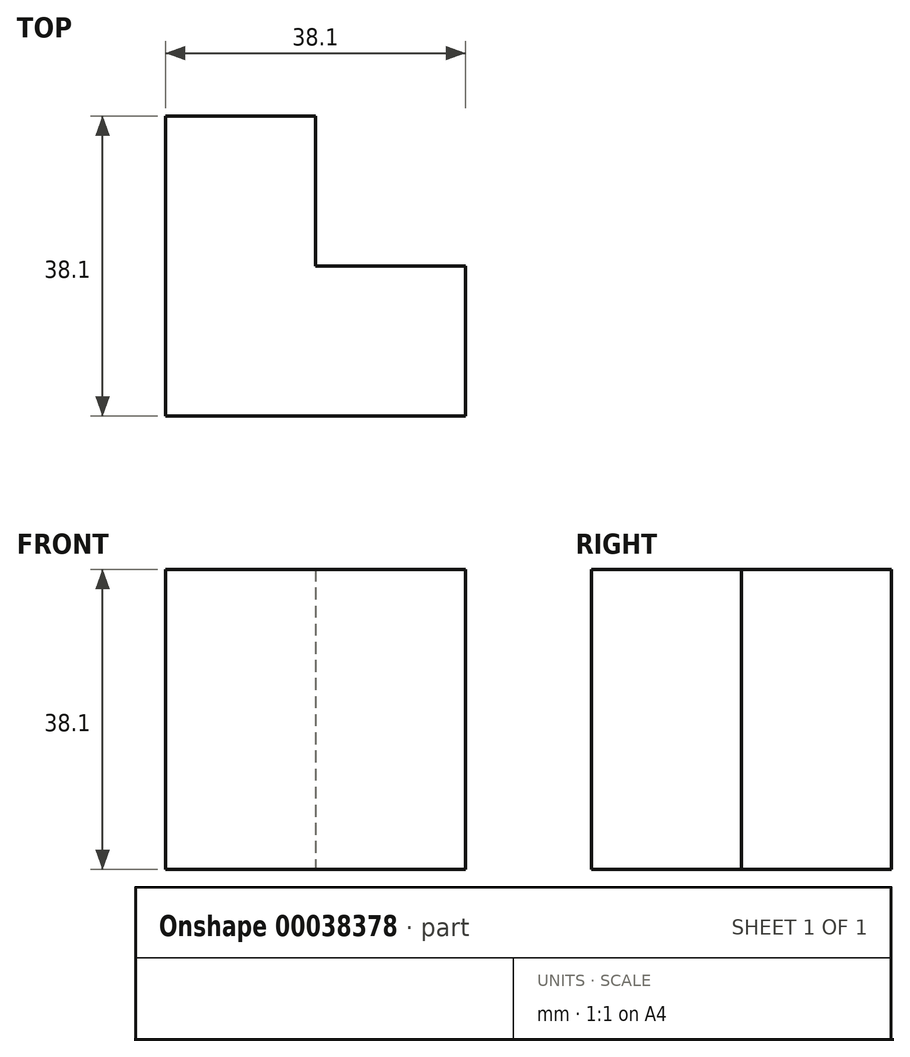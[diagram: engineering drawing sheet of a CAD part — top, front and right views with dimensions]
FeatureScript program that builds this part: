
annotation { "Feature Type Name" : "Feature", "Feature Type Description" : "" }
export const myFeature = defineFeature(function(context is Context, id is Id, definition is map)
    precondition{}
    {
        {
            var Q0;
            Q0=qCreatedBy(makeId("Top.planeOp"),FACE);
            var sketch = newSketch(context, id + "F0", { "sketchPlane" : qUnion([Q0])});
            skLineSegment(sketch, "E0.bottom", {"start": v(0, 0) * mm, "end": v(19.05, 0) * mm});
            skLineSegment(sketch, "E0.top", {"start": v(0, 19.05) * mm, "end": v(19.05, 19.05) * mm});
            skLineSegment(sketch, "E0.left", {"start": v(0, 0) * mm, "end": v(0, 19.05) * mm});
            skLineSegment(sketch, "E0.right", {"start": v(19.05, 0) * mm, "end": v(19.05, 19.05) * mm});
            skSolve(sketch);
        }
        {
            var Q0;
            Q0=makeQuery(id+"F0.imprint","IMPRINT",FACE,{"disambiguationData":[TD([[makeQuery(id+"F0.imprint","IMPRINT",EDGE,{"derivedFrom":sQuery(id+"F0.wireOp",EDGE,"E0.bottom")}),1.0]])]});
            extrude(context, id + "F1", {"entities" : qUnion([Q0]), "depth" : 19.05 * mm});
        }
        {
            var Q0;
            Q0=makeQuery(id+"F1.opExtrude","SWEPT_FACE",FACE,{"disambiguationData":[OSD([sQuery(id+"F0.wireOp",EDGE,"E0.top")])]});
            extrude(context, id + "F2", {"entities" : qUnion([Q0]), "operationType" : NewBodyOperationType.ADD, "depth" : 19.05 * mm});
        }
        {
            var Q0;
            {var subQ0=sQuery(id+"F0.wireOp",EDGE,"E0.top");Q0=makeQuery(id+"F2.boolean.opBoolean","MERGE",FACE,{"derivedFrom":[makeQuery(id+"F1.opExtrude","CAP_FACE",FACE,{"disambiguationData":[OSD([sQuery(id+"F0.wireOp",EDGE,"E0.bottom"),subQ0,sQuery(id+"F0.wireOp",EDGE,"E0.left"),sQuery(id+"F0.wireOp",EDGE,"E0.right")])],"isStart":false}),makeQuery(id+"F2.opExtrude","SWEPT_FACE",FACE,{"disambiguationData":[OSD([subQ0]),TDD([makeQuery(id+"F1.opExtrude","CAP_EDGE",EDGE,{"disambiguationData":[OSD([subQ0])],"isStart":false})])]})]});}
            var sketch = newSketch(context, id + "F3", { "sketchPlane" : qUnion([Q0])});
            skLineSegment(sketch, "E1.bottom", {"start": v(19.05, 19.05) * mm, "end": v(0, 19.05) * mm});
            skLineSegment(sketch, "E1.top", {"start": v(19.05, 38.1) * mm, "end": v(0, 38.1) * mm});
            skLineSegment(sketch, "E1.left", {"start": v(19.05, 19.05) * mm, "end": v(19.05, 38.1) * mm});
            skLineSegment(sketch, "E1.right", {"start": v(0, 19.05) * mm, "end": v(0, 38.1) * mm});
            skLineSegment(sketch, "E2.top", {"start": v(19.05, 0) * mm, "end": v(0, 0) * mm});
            skLineSegment(sketch, "E2.left", {"start": v(19.05, 19.05) * mm, "end": v(19.05, 0) * mm});
            skLineSegment(sketch, "E2.right", {"start": v(0, 19.05) * mm, "end": v(0, 0) * mm});
            skSolve(sketch);
        }
        {
            var Q0;
            {var subQ0=sQuery(id+"F0.wireOp",EDGE,"E0.right");Q0=makeQuery(id+"F2.boolean.opBoolean","MERGE",FACE,{"derivedFrom":[makeQuery(id+"F1.opExtrude","SWEPT_FACE",FACE,{"disambiguationData":[OSD([subQ0])]}),makeQuery(id+"F2.opExtrude","SWEPT_FACE",FACE,{"disambiguationData":[OSD([sQuery(id+"F0.wireOp",EDGE,"E0.top"),subQ0])]})]});}
            var sketch = newSketch(context, id + "F4", { "sketchPlane" : qUnion([Q0])});
            skLineSegment(sketch, "E3.bottom", {"start": v(19.05, 19.05) * mm, "end": v(0, 19.05) * mm});
            skLineSegment(sketch, "E3.top", {"start": v(19.05, 0) * mm, "end": v(0, 0) * mm});
            skLineSegment(sketch, "E3.left", {"start": v(19.05, 19.05) * mm, "end": v(19.05, 0) * mm});
            skLineSegment(sketch, "E3.right", {"start": v(0, 19.05) * mm, "end": v(0, 0) * mm});
            skSolve(sketch);
        }
        {
            var Q0;
            Q0=makeQuery(id+"F4.imprint","IMPRINT",FACE,{"disambiguationData":[TD([[makeQuery(id+"F4.imprint","IMPRINT",EDGE,{"derivedFrom":sQuery(id+"F4.wireOp",EDGE,"E3.bottom")}),-1.0]])]});
            extrude(context, id + "F5", {"entities" : qUnion([Q0]), "operationType" : NewBodyOperationType.ADD, "depth" : 19.05 * mm});
        }
        {
            var Q0;
            Q0=makeQuery(id+"F3.imprint","IMPRINT",FACE,{"disambiguationData":[TD([[makeQuery(id+"F3.imprint","IMPRINT",EDGE,{"derivedFrom":sQuery(id+"F3.wireOp",EDGE,"E1.bottom")}),1.0]])]});
            extrude(context, id + "F6", {"entities" : qUnion([Q0]), "operationType" : NewBodyOperationType.ADD, "depth" : 19.05 * mm});
        }
        {
            var Q0;
            Q0=makeQuery(id+"F6.opExtrude","SWEPT_FACE",FACE,{"disambiguationData":[OSD([sQuery(id+"F3.wireOp",EDGE,"E2.left")])]});
            extrude(context, id + "F7", {"entities" : qUnion([Q0]), "operationType" : NewBodyOperationType.ADD, "depth" : 19.05 * mm});
        }
        {
            var Q0;
            {var subQ0=sQuery(id+"F0.wireOp",EDGE,"E0.top");var subQ1=sQuery(id+"F0.wireOp",EDGE,"E0.left");var subQ2=sQuery(id+"F0.wireOp",EDGE,"E0.right");var subQ3=makeQuery(id+"F1.opExtrude","CAP_FACE",FACE,{"disambiguationData":[OSD([sQuery(id+"F0.wireOp",EDGE,"E0.bottom"),subQ0,subQ1,subQ2])],"isStart":false});var subQ4=makeQuery(id+"F2.opExtrude","SWEPT_FACE",FACE,{"disambiguationData":[OSD([subQ0]),TDD([makeQuery(id+"F1.opExtrude","CAP_EDGE",EDGE,{"disambiguationData":[OSD([subQ0])],"isStart":false})])]});var subQ5=makeQuery(id+"F5.opExtrude","SWEPT_FACE",FACE,{"disambiguationData":[OSD([sQuery(id+"F4.wireOp",EDGE,"E3.bottom")])]});Q0=makeQuery(id+"F6.boolean.opBoolean","SPLIT",FACE,{"disambiguationData":[TD([makeQuery(id+"F1.opExtrude","SWEPT_FACE",FACE,{"disambiguationData":[OSD([subQ1])]})])],"derivedFrom":makeQuery(id+"F5.boolean.opBoolean","MERGE",FACE,{"derivedFrom":[makeQuery(id+"F2.boolean.opBoolean","MERGE",FACE,{"derivedFrom":[subQ3,subQ4]}),subQ5]})});}
            extrude(context, id + "F8", {"entities" : qUnion([Q0]), "operationType" : NewBodyOperationType.ADD, "depth" : 19.05 * mm});
        }
    });
